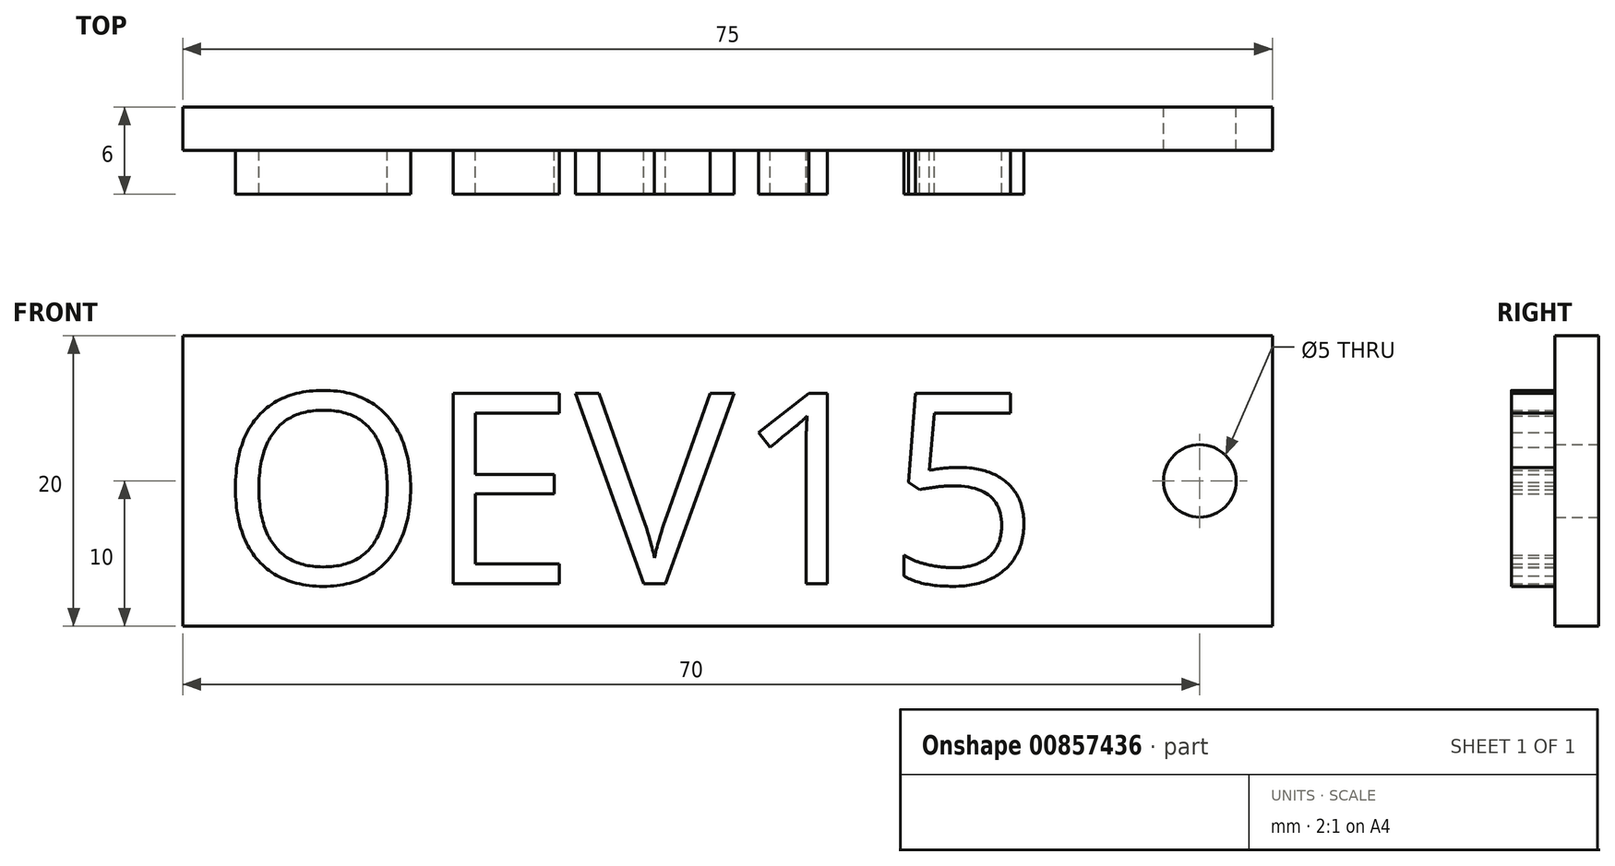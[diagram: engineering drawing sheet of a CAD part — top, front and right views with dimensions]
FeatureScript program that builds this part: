
annotation { "Feature Type Name" : "Feature", "Feature Type Description" : "" }
export const myFeature = defineFeature(function(context is Context, id is Id, definition is map)
    precondition{}
    {
        {
            var Q0;
            Q0=qCreatedBy(makeId("Front.planeOp"),FACE);
            var sketch = newSketch(context, id + "F0", { "sketchPlane" : qUnion([Q0])});
            skLineSegment(sketch, "E0.bottom", {"start": v(0, 0) * mm, "end": v(75, 0) * mm});
            skLineSegment(sketch, "E0.top", {"start": v(0, -20) * mm, "end": v(75, -20) * mm});
            skLineSegment(sketch, "E0.left", {"start": v(0, 0) * mm, "end": v(0, -20) * mm});
            skLineSegment(sketch, "E0.right", {"start": v(75, 0) * mm, "end": v(75, -20) * mm});
            skCircle(sketch, "E1", {"center": v(70, -10) * mm, "radius": 2.5 * mm});
            skSolve(sketch);
        }
        {
            var Q0;
            Q0 = qSketchRegion(id + "F0", true);
            extrude(context, id + "F1", {"entities" : qUnion([Q0]), "depth" : 3 * mm, "offsetDistance" : 25 * mm});
        }
        {
            var Q0;
            Q0=makeQuery(id+"F1.opExtrude","CAP_FACE",FACE,{"disambiguationData":[OSD([sQuery(id+"F0.wireOp",EDGE,"E0.bottom"),sQuery(id+"F0.wireOp",EDGE,"E0.top"),sQuery(id+"F0.wireOp",EDGE,"E0.left"),sQuery(id+"F0.wireOp",EDGE,"E0.right"),sQuery(id+"F0.wireOp",EDGE,"E1")])],"isStart":false});
            var sketch = newSketch(context, id + "F2", { "sketchPlane" : qUnion([Q0])});
            skText(sketch, "E2", { "text": "OEV15", "fontName": "OpenSans-Regular.ttf"});
            const initialGuessF2  = {"E2": [0.00251, -0.01708, 1, 0, 0.01322]};
            skSetInitialGuess(sketch, initialGuessF2);
            skSolve(sketch);
        }
        {
            var Q0;
            Q0 = qSketchRegion(id + "F2", true);
            extrude(context, id + "F3", {"entities" : qUnion([Q0]), "operationType" : NewBodyOperationType.ADD, "depth" : 3 * mm, "offsetDistance" : 25 * mm});
        }
    });
